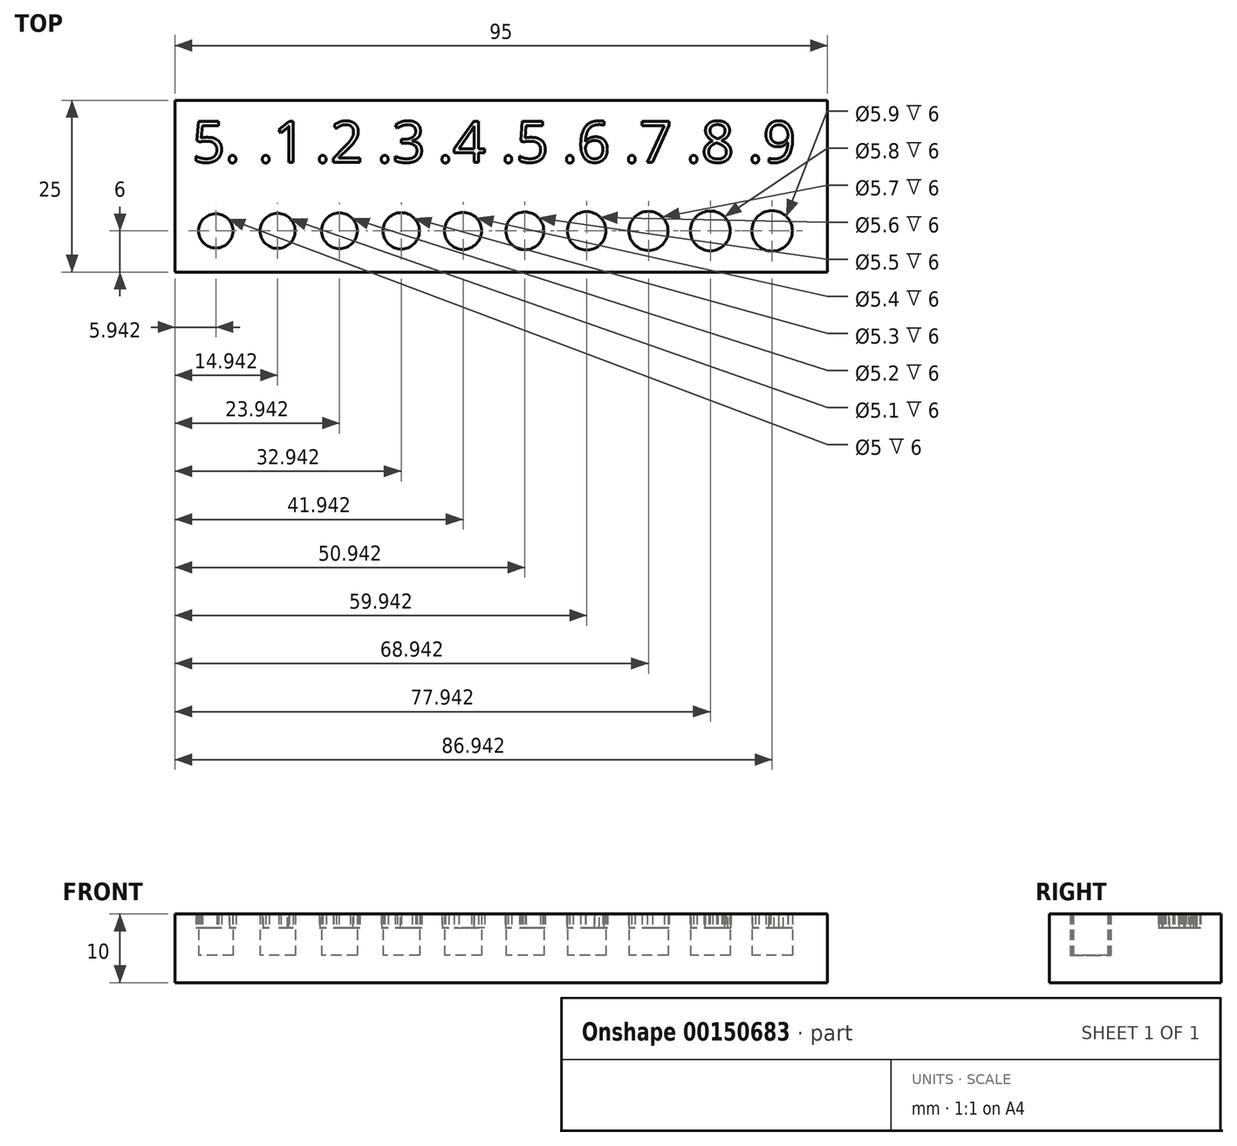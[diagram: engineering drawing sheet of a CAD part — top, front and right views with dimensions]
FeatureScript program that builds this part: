
annotation { "Feature Type Name" : "Feature", "Feature Type Description" : "" }
export const myFeature = defineFeature(function(context is Context, id is Id, definition is map)
    precondition{}
    {
        {
            var Q0;
            Q0=qCreatedBy(makeId("Top.planeOp"),FACE);
            var sketch = newSketch(context, id + "F0", { "sketchPlane" : qUnion([Q0])});
            skLineSegment(sketch, "E0.bottom", {"start": v(0, 0) * mm, "end": v(95, 0) * mm});
            skLineSegment(sketch, "E0.top", {"start": v(0, 25) * mm, "end": v(95, 25) * mm});
            skLineSegment(sketch, "E0.left", {"start": v(0, 0) * mm, "end": v(0, 25) * mm});
            skLineSegment(sketch, "E0.right", {"start": v(95, 0) * mm, "end": v(95, 25) * mm});
            skCircle(sketch, "E1", {"center": v(5.94, 6) * mm, "radius": 2.5 * mm});
            skCircle(sketch, "E2", {"center": v(14.94, 6) * mm, "radius": 2.55 * mm});
            skCircle(sketch, "E3", {"center": v(23.94, 6) * mm, "radius": 2.6 * mm});
            skCircle(sketch, "E4", {"center": v(32.94, 6) * mm, "radius": 2.65 * mm});
            skCircle(sketch, "E5", {"center": v(41.94, 6) * mm, "radius": 2.7 * mm});
            skCircle(sketch, "E6", {"center": v(50.94, 6) * mm, "radius": 2.75 * mm});
            skCircle(sketch, "E7", {"center": v(59.94, 6) * mm, "radius": 2.8 * mm});
            skCircle(sketch, "E8", {"center": v(68.94, 6) * mm, "radius": 2.85 * mm});
            skCircle(sketch, "E9", {"center": v(77.94, 6) * mm, "radius": 2.9 * mm});
            skCircle(sketch, "E10", {"center": v(86.94, 6) * mm, "radius": 2.95 * mm});
            skText(sketch, "E11", { "text": "5.", "fontName": "OpenSans-Regular.ttf"});
            skText(sketch, "E12", { "text": ".1", "fontName": "OpenSans-Regular.ttf"});
            skLineSegment(sketch, "E13", {"start": v(0, 16) * mm, "end": v(95, 16) * mm, "construction": true});
            skText(sketch, "E14", { "text": ".2", "fontName": "OpenSans-Regular.ttf"});
            skText(sketch, "E15", { "text": ".3", "fontName": "OpenSans-Regular.ttf"});
            skText(sketch, "E16", { "text": ".4", "fontName": "OpenSans-Regular.ttf"});
            skText(sketch, "E17", { "text": ".5", "fontName": "OpenSans-Regular.ttf"});
            skText(sketch, "E18", { "text": ".6", "fontName": "OpenSans-Regular.ttf"});
            skText(sketch, "E19", { "text": ".7", "fontName": "OpenSans-Regular.ttf"});
            skText(sketch, "E20", { "text": ".8", "fontName": "OpenSans-Regular.ttf"});
            skText(sketch, "E21", { "text": ".9", "fontName": "OpenSans-Regular.ttf"});
            const initialGuessF0  = {"E11": [0.0025, 0.016, 1, 0, 0.006], "E12": [0.0121, 0.016, 1, 0, 0.006], "E14": [0.0204, 0.016, 1, 0, 0.006], "E15": [0.02943, 0.016, 1, 0, 0.006], "E16": [0.03826, 0.016, 1, 0, 0.006], "E17": [0.04742, 0.016, 1, 0, 0.006], "E18": [0.05638, 0.016, 1, 0, 0.006], "E19": [0.0654, 0.016, 1, 0, 0.006], "E20": [0.0744, 0.016, 1, 0, 0.006], "E21": [0.0834, 0.016, 1, 0, 0.006]};
            skSetInitialGuess(sketch, initialGuessF0);
            skSolve(sketch);
        }
        {
            var Q0;
            Q0=makeQuery(id+"F0.imprint","IMPRINT",FACE,{"disambiguationData":[TD([[makeQuery(id+"F0.imprint","IMPRINT",EDGE,{"derivedFrom":sQuery(id+"F0.wireOp",EDGE,"E0.bottom")}),1.0]])]});
            var Q1;
            Q1=makeQuery(id+"F0.imprint","IMPRINT",FACE,{"disambiguationData":[TD([[makeQuery(id+"F0.imprint","IMPRINT",EDGE,{"derivedFrom":sQuery(id+"F0.wireOp",EDGE,"E10")}),1.0]])]});
            var Q2;
            Q2=makeQuery(id+"F0.imprint","IMPRINT",FACE,{"disambiguationData":[TD([[makeQuery(id+"F0.imprint","IMPRINT",EDGE,{"derivedFrom":sQuery(id+"F0.wireOp",EDGE,"E9")}),1.0]])]});
            var Q3;
            Q3=makeQuery(id+"F0.imprint","IMPRINT",FACE,{"disambiguationData":[TD([[makeQuery(id+"F0.imprint","IMPRINT",EDGE,{"derivedFrom":sQuery(id+"F0.wireOp",EDGE,"E8")}),1.0]])]});
            var Q4;
            Q4 = qSketchRegion(id + "F0", true);
            var Q5;
            Q5=makeQuery(id+"F0.imprint","IMPRINT",FACE,{"disambiguationData":[TD([[makeQuery(id+"F0.imprint","IMPRINT",EDGE,{"derivedFrom":sQuery(id+"F0.wireOp",EDGE,"E7")}),1.0]])]});
            var Q6;
            Q6=makeQuery(id+"F0.imprint","IMPRINT",FACE,{"disambiguationData":[TD([[makeQuery(id+"F0.imprint","IMPRINT",EDGE,{"derivedFrom":sQuery(id+"F0.wireOp",EDGE,"E20.sketch_text.stroke-23")}),1.0]])]});
            var Q7;
            Q7=makeQuery(id+"F0.imprint","IMPRINT",FACE,{"disambiguationData":[TD([[makeQuery(id+"F0.imprint","IMPRINT",EDGE,{"derivedFrom":sQuery(id+"F0.wireOp",EDGE,"E6")}),1.0]])]});
            var Q8;
            Q8=makeQuery(id+"F0.imprint","IMPRINT",FACE,{"disambiguationData":[TD([[makeQuery(id+"F0.imprint","IMPRINT",EDGE,{"derivedFrom":sQuery(id+"F0.wireOp",EDGE,"E5")}),1.0]])]});
            var Q9;
            Q9=makeQuery(id+"F0.imprint","IMPRINT",FACE,{"disambiguationData":[TD([[makeQuery(id+"F0.imprint","IMPRINT",EDGE,{"derivedFrom":sQuery(id+"F0.wireOp",EDGE,"E18.sketch_text.stroke-23")}),1.0]])]});
            var Q10;
            Q10=makeQuery(id+"F0.imprint","IMPRINT",FACE,{"disambiguationData":[TD([[makeQuery(id+"F0.imprint","IMPRINT",EDGE,{"derivedFrom":sQuery(id+"F0.wireOp",EDGE,"E4")}),1.0]])]});
            var Q11;
            Q11=makeQuery(id+"F0.imprint","IMPRINT",FACE,{"disambiguationData":[TD([[makeQuery(id+"F0.imprint","IMPRINT",EDGE,{"derivedFrom":sQuery(id+"F0.wireOp",EDGE,"E3")}),1.0]])]});
            var Q12;
            Q12=makeQuery(id+"F0.imprint","IMPRINT",FACE,{"disambiguationData":[TD([[makeQuery(id+"F0.imprint","IMPRINT",EDGE,{"derivedFrom":sQuery(id+"F0.wireOp",EDGE,"E16.sketch_text.stroke-19")}),1.0]])]});
            var Q13;
            Q13=makeQuery(id+"F0.imprint","IMPRINT",FACE,{"disambiguationData":[TD([[makeQuery(id+"F0.imprint","IMPRINT",EDGE,{"derivedFrom":sQuery(id+"F0.wireOp",EDGE,"E2")}),1.0]])]});
            var Q14;
            Q14=makeQuery(id+"F0.imprint","IMPRINT",FACE,{"disambiguationData":[TD([[makeQuery(id+"F0.imprint","IMPRINT",EDGE,{"derivedFrom":sQuery(id+"F0.wireOp",EDGE,"E1")}),1.0]])]});
            var Q15;
            Q15=makeQuery(id+"F0.imprint","IMPRINT",FACE,{"disambiguationData":[TD([[makeQuery(id+"F0.imprint","IMPRINT",EDGE,{"derivedFrom":sQuery(id+"F0.wireOp",EDGE,"E21.sketch_text.stroke-8")}),-1.0]])]});
            var Q16;
            Q16=makeQuery(id+"F0.imprint","IMPRINT",FACE,{"disambiguationData":[TD([[makeQuery(id+"F0.imprint","IMPRINT",EDGE,{"derivedFrom":sQuery(id+"F0.wireOp",EDGE,"E21.sketch_text.stroke-0")}),-1.0]])]});
            var Q17;
            Q17=makeQuery(id+"F0.imprint","IMPRINT",FACE,{"disambiguationData":[TD([[makeQuery(id+"F0.imprint","IMPRINT",EDGE,{"derivedFrom":sQuery(id+"F0.wireOp",EDGE,"E21.sketch_text.stroke-24")}),1.0]])]});
            var Q18;
            Q18=makeQuery(id+"F0.imprint","IMPRINT",FACE,{"disambiguationData":[TD([[makeQuery(id+"F0.imprint","IMPRINT",EDGE,{"derivedFrom":sQuery(id+"F0.wireOp",EDGE,"E20.sketch_text.stroke-8")}),-1.0]])]});
            var Q19;
            Q19=makeQuery(id+"F0.imprint","IMPRINT",FACE,{"disambiguationData":[TD([[makeQuery(id+"F0.imprint","IMPRINT",EDGE,{"derivedFrom":sQuery(id+"F0.wireOp",EDGE,"E20.sketch_text.stroke-31")}),1.0]])]});
            var Q20;
            Q20=makeQuery(id+"F0.imprint","IMPRINT",FACE,{"disambiguationData":[TD([[makeQuery(id+"F0.imprint","IMPRINT",EDGE,{"derivedFrom":sQuery(id+"F0.wireOp",EDGE,"E19.sketch_text.stroke-8")}),-1.0]])]});
            var Q21;
            Q21=makeQuery(id+"F0.imprint","IMPRINT",FACE,{"disambiguationData":[TD([[makeQuery(id+"F0.imprint","IMPRINT",EDGE,{"derivedFrom":sQuery(id+"F0.wireOp",EDGE,"E18.sketch_text.stroke-8")}),-1.0]])]});
            var Q22;
            Q22=makeQuery(id+"F0.imprint","IMPRINT",FACE,{"disambiguationData":[TD([[makeQuery(id+"F0.imprint","IMPRINT",EDGE,{"derivedFrom":sQuery(id+"F0.wireOp",EDGE,"E17.sketch_text.stroke-8")}),-1.0]])]});
            var Q23;
            Q23=makeQuery(id+"F0.imprint","IMPRINT",FACE,{"disambiguationData":[TD([[makeQuery(id+"F0.imprint","IMPRINT",EDGE,{"derivedFrom":sQuery(id+"F0.wireOp",EDGE,"E17.sketch_text.stroke-0")}),-1.0]])]});
            var Q24;
            Q24=makeQuery(id+"F0.imprint","IMPRINT",FACE,{"disambiguationData":[TD([[makeQuery(id+"F0.imprint","IMPRINT",EDGE,{"derivedFrom":sQuery(id+"F0.wireOp",EDGE,"E16.sketch_text.stroke-8")}),-1.0]])]});
            var Q25;
            Q25=makeQuery(id+"F0.imprint","IMPRINT",FACE,{"disambiguationData":[TD([[makeQuery(id+"F0.imprint","IMPRINT",EDGE,{"derivedFrom":sQuery(id+"F0.wireOp",EDGE,"E15.sketch_text.stroke-8")}),-1.0]])]});
            var Q26;
            Q26=makeQuery(id+"F0.imprint","IMPRINT",FACE,{"disambiguationData":[TD([[makeQuery(id+"F0.imprint","IMPRINT",EDGE,{"derivedFrom":sQuery(id+"F0.wireOp",EDGE,"E14.sketch_text.stroke-8")}),-1.0]])]});
            var Q27;
            Q27=makeQuery(id+"F0.imprint","IMPRINT",FACE,{"disambiguationData":[TD([[makeQuery(id+"F0.imprint","IMPRINT",EDGE,{"derivedFrom":sQuery(id+"F0.wireOp",EDGE,"E12.sketch_text.stroke-0")}),-1.0]])]});
            var Q28;
            Q28=makeQuery(id+"F0.imprint","IMPRINT",FACE,{"disambiguationData":[TD([[makeQuery(id+"F0.imprint","IMPRINT",EDGE,{"derivedFrom":sQuery(id+"F0.wireOp",EDGE,"E12.sketch_text.stroke-8")}),-1.0]])]});
            var Q29;
            Q29=makeQuery(id+"F0.imprint","IMPRINT",FACE,{"disambiguationData":[TD([[makeQuery(id+"F0.imprint","IMPRINT",EDGE,{"derivedFrom":sQuery(id+"F0.wireOp",EDGE,"E11.sketch_text.stroke-0")}),-1.0]])]});
            var Q30;
            Q30=makeQuery(id+"F0.imprint","IMPRINT",FACE,{"disambiguationData":[TD([[makeQuery(id+"F0.imprint","IMPRINT",EDGE,{"derivedFrom":sQuery(id+"F0.wireOp",EDGE,"E16.sketch_text.stroke-0")}),-1.0]])]});
            var Q31;
            Q31=makeQuery(id+"F0.imprint","IMPRINT",FACE,{"disambiguationData":[TD([[makeQuery(id+"F0.imprint","IMPRINT",EDGE,{"derivedFrom":sQuery(id+"F0.wireOp",EDGE,"E15.sketch_text.stroke-0")}),-1.0]])]});
            var Q32;
            Q32=makeQuery(id+"F0.imprint","IMPRINT",FACE,{"disambiguationData":[TD([[makeQuery(id+"F0.imprint","IMPRINT",EDGE,{"derivedFrom":sQuery(id+"F0.wireOp",EDGE,"E20.sketch_text.stroke-0")}),-1.0]])]});
            var Q33;
            Q33=makeQuery(id+"F0.imprint","IMPRINT",FACE,{"disambiguationData":[TD([[makeQuery(id+"F0.imprint","IMPRINT",EDGE,{"derivedFrom":sQuery(id+"F0.wireOp",EDGE,"E19.sketch_text.stroke-0")}),-1.0]])]});
            var Q34;
            Q34=makeQuery(id+"F0.imprint","IMPRINT",FACE,{"disambiguationData":[TD([[makeQuery(id+"F0.imprint","IMPRINT",EDGE,{"derivedFrom":sQuery(id+"F0.wireOp",EDGE,"E14.sketch_text.stroke-0")}),-1.0]])]});
            var Q35;
            Q35=makeQuery(id+"F0.imprint","IMPRINT",FACE,{"disambiguationData":[TD([[makeQuery(id+"F0.imprint","IMPRINT",EDGE,{"derivedFrom":sQuery(id+"F0.wireOp",EDGE,"E18.sketch_text.stroke-0")}),-1.0]])]});
            var Q36;
            Q36=makeQuery(id+"F0.imprint","IMPRINT",FACE,{"disambiguationData":[TD([[makeQuery(id+"F0.imprint","IMPRINT",EDGE,{"derivedFrom":sQuery(id+"F0.wireOp",EDGE,"E11.sketch_text.stroke-19")}),-1.0]])]});
            extrude(context, id + "F1", {"entities" : qUnion([Q0, Q1, Q2, Q3, Q4, Q5, Q6, Q7, Q8, Q9, Q10, Q11, Q12, Q13, Q14, Q15, Q16, Q17, Q18, Q19, Q20, Q21, Q22, Q23, Q24, Q25, Q26, Q27, Q28, Q29, Q30, Q31, Q32, Q33, Q34, Q35, Q36]), "oppositeDirection" : true, "depth" : 8 * mm});
        }
        {
            var Q0;
            Q0 = qSketchRegion(id + "F0", true);
            var Q1;
            Q1=makeQuery(id+"F0.imprint","IMPRINT",FACE,{"disambiguationData":[TD([[makeQuery(id+"F0.imprint","IMPRINT",EDGE,{"derivedFrom":sQuery(id+"F0.wireOp",EDGE,"E18.sketch_text.stroke-23")}),1.0]])]});
            var Q2;
            Q2=makeQuery(id+"F0.imprint","IMPRINT",FACE,{"disambiguationData":[TD([[makeQuery(id+"F0.imprint","IMPRINT",EDGE,{"derivedFrom":sQuery(id+"F0.wireOp",EDGE,"E20.sketch_text.stroke-23")}),1.0]])]});
            var Q3;
            Q3=makeQuery(id+"F0.imprint","IMPRINT",FACE,{"disambiguationData":[TD([[makeQuery(id+"F0.imprint","IMPRINT",EDGE,{"derivedFrom":sQuery(id+"F0.wireOp",EDGE,"E20.sketch_text.stroke-31")}),1.0]])]});
            var Q4;
            Q4=makeQuery(id+"F0.imprint","IMPRINT",FACE,{"disambiguationData":[TD([[makeQuery(id+"F0.imprint","IMPRINT",EDGE,{"derivedFrom":sQuery(id+"F0.wireOp",EDGE,"E21.sketch_text.stroke-24")}),1.0]])]});
            var Q5;
            Q5=makeQuery(id+"F0.imprint","IMPRINT",FACE,{"disambiguationData":[TD([[makeQuery(id+"F0.imprint","IMPRINT",EDGE,{"derivedFrom":sQuery(id+"F0.wireOp",EDGE,"E16.sketch_text.stroke-19")}),1.0]])]});
            extrude(context, id + "F2", {"entities" : qUnion([Q0, Q1, Q2, Q3, Q4, Q5]), "operationType" : NewBodyOperationType.ADD, "depth" : 2 * mm});
        }
        {
            var Q0;
            Q0=makeQuery(id+"F0.imprint","IMPRINT",FACE,{"disambiguationData":[TD([[makeQuery(id+"F0.imprint","IMPRINT",EDGE,{"derivedFrom":sQuery(id+"F0.wireOp",EDGE,"E1")}),1.0]])]});
            var Q1;
            Q1=makeQuery(id+"F0.imprint","IMPRINT",FACE,{"disambiguationData":[TD([[makeQuery(id+"F0.imprint","IMPRINT",EDGE,{"derivedFrom":sQuery(id+"F0.wireOp",EDGE,"E2")}),1.0]])]});
            var Q2;
            Q2=makeQuery(id+"F0.imprint","IMPRINT",FACE,{"disambiguationData":[TD([[makeQuery(id+"F0.imprint","IMPRINT",EDGE,{"derivedFrom":sQuery(id+"F0.wireOp",EDGE,"E3")}),1.0]])]});
            var Q3;
            Q3=makeQuery(id+"F0.imprint","IMPRINT",FACE,{"disambiguationData":[TD([[makeQuery(id+"F0.imprint","IMPRINT",EDGE,{"derivedFrom":sQuery(id+"F0.wireOp",EDGE,"E4")}),1.0]])]});
            var Q4;
            Q4=makeQuery(id+"F0.imprint","IMPRINT",FACE,{"disambiguationData":[TD([[makeQuery(id+"F0.imprint","IMPRINT",EDGE,{"derivedFrom":sQuery(id+"F0.wireOp",EDGE,"E5")}),1.0]])]});
            var Q5;
            Q5=makeQuery(id+"F0.imprint","IMPRINT",FACE,{"disambiguationData":[TD([[makeQuery(id+"F0.imprint","IMPRINT",EDGE,{"derivedFrom":sQuery(id+"F0.wireOp",EDGE,"E6")}),1.0]])]});
            var Q6;
            Q6=makeQuery(id+"F0.imprint","IMPRINT",FACE,{"disambiguationData":[TD([[makeQuery(id+"F0.imprint","IMPRINT",EDGE,{"derivedFrom":sQuery(id+"F0.wireOp",EDGE,"E7")}),1.0]])]});
            var Q7;
            Q7=makeQuery(id+"F0.imprint","IMPRINT",FACE,{"disambiguationData":[TD([[makeQuery(id+"F0.imprint","IMPRINT",EDGE,{"derivedFrom":sQuery(id+"F0.wireOp",EDGE,"E8")}),1.0]])]});
            var Q8;
            Q8=makeQuery(id+"F0.imprint","IMPRINT",FACE,{"disambiguationData":[TD([[makeQuery(id+"F0.imprint","IMPRINT",EDGE,{"derivedFrom":sQuery(id+"F0.wireOp",EDGE,"E9")}),1.0]])]});
            var Q9;
            Q9=makeQuery(id+"F0.imprint","IMPRINT",FACE,{"disambiguationData":[TD([[makeQuery(id+"F0.imprint","IMPRINT",EDGE,{"derivedFrom":sQuery(id+"F0.wireOp",EDGE,"E10")}),1.0]])]});
            extrude(context, id + "F3", {"entities" : qUnion([Q0, Q1, Q2, Q3, Q4, Q5, Q6, Q7, Q8, Q9]), "operationType" : NewBodyOperationType.REMOVE, "oppositeDirection" : true, "depth" : 4 * mm});
        }
        {
            var Q0;
            Q0=makeQuery(id+"F1.opExtrude","SWEPT_BODY",BODY,{"disambiguationData":[OSD([sQuery(id+"F0.wireOp",EDGE,"E0.bottom"),sQuery(id+"F0.wireOp",EDGE,"E0.top"),sQuery(id+"F0.wireOp",EDGE,"E0.left"),sQuery(id+"F0.wireOp",EDGE,"E0.right")])]});
            transform(context, id + "F4", {"entities" : qUnion([Q0]), "transformType" : TransformType.TRANSLATION_3D, "dx" : 0 * mm, "dy" : 0 * mm, "dz" : 8 * mm, "makeCopy" : false});
        }
    });
